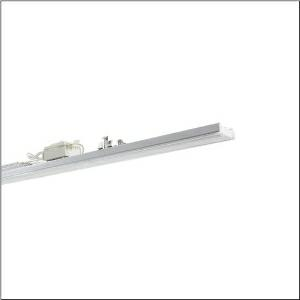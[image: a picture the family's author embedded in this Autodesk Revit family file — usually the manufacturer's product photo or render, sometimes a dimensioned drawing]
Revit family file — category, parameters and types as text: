
# Revit family: licross_r__11_recessed_mo_51tl14dn325g_7428
name_source: partatom
category: Lighting Fixtures
units: mm (PartAtom-declared; Revit-internal decimal feet)

## family parameters
Cut with Voids When Loaded = No
Host = Face
Light Source = No
Part Type = Normal
Room Calculation Point = No
Round Connector Dimension = Use Diameter
Shared = No

## types (1)
- --- (1 x LED, 2900 lm, 17.6 W, 3000K)
    Apparent Load = 18 VA
    CIE Flux Codes = 56 84 97 100 100
    Color Rendering = 80
    Color Temperature = 3000K
    Default Elevation = 1800 mm
    Description = Licross® 11 Recessed MO, luminaire insert, of sheet steel, coil coated, white, length: 1.500mm, width: 66mm, height: 67mm, LED rated luminous flux: 2.900lm, light colour: 830, control gear: DALI 2, with plug, 5-pole, with phase selection, mains connection: 220..240V, AC, 50/60Hz, rated input power: 17.6W, halogen-free wiring, primary light control with lens, of plastic, primary optical cover: cover, of PMMA, light emission: direct distribution, primary light characteristic: asymmetric, protection rating (complete): IP40, insulation class (complete): insulation class I (protective earthing), certification: CE, ENEC, VDE, UKCA, protection symbol: D if used in an environment without relevant dust loads with corresponding accessories, impact resistance: IK06, permissible ambient temperature for indoor applications: -25..+50°C, corresponds to IFS (International Featured Standards) requirements for safety and quality in the food industry, reducing of maximum allowable ambient temperature of 5°C with ceiling mounting, LABS conformity tested according to VDMA 24364:2018-05, packaging unit: 1 piece
    Height = 58 mm
    Lamp = 1 x LED
    Lamp Light Flux = 2900 lm
    Lamp Power = 17.6 W
    Lamp count = 1
    Length = 1500 mm
    Luminous efficacy = 165 lm/W
    Manufacturer = Siteco
    ModVariant = No
    Model = 51TL14DN325G
    Mounting Place = Ceiling
    Mounting Type = Pendant
    Number of Poles = 1
    OnlyDefault = Yes
    Power Factor = 1
    Product Name = Licross® 11 Recessed MO
    Product group = luminaire insert
    ProductGroupID = 902
    Protection Class = Protection class I
    Protection Degree = IP 40
    RLX_Detail_Level = 1
    RLX_Emergency_Light_Flux = 0 lm
    RLX_Emergency_Type = 0
    RLX_Emergency_Type_DB = No
    RlxData = <blob elided: 24589 chars, md5=10165ee3>
    Socket = socket
    Standby Power = 0 W
    System Light Flux = 2900 lm
    System Power = 18 W
    Type Comments = factory setting: luminous flux: 100 % | dim-lin: 254 | 114 mA
    Type Image = l_1296930.jpg
    URL = http://relux.com
    VarID = @adj_068038
    Voltage = 0 V
    Weight = 0.00 kg
    Width = 66 mm

## geometry (parser evidence)
native form markers: Blend x4, Sweep x10
no freeform markers — native parametric forms only
